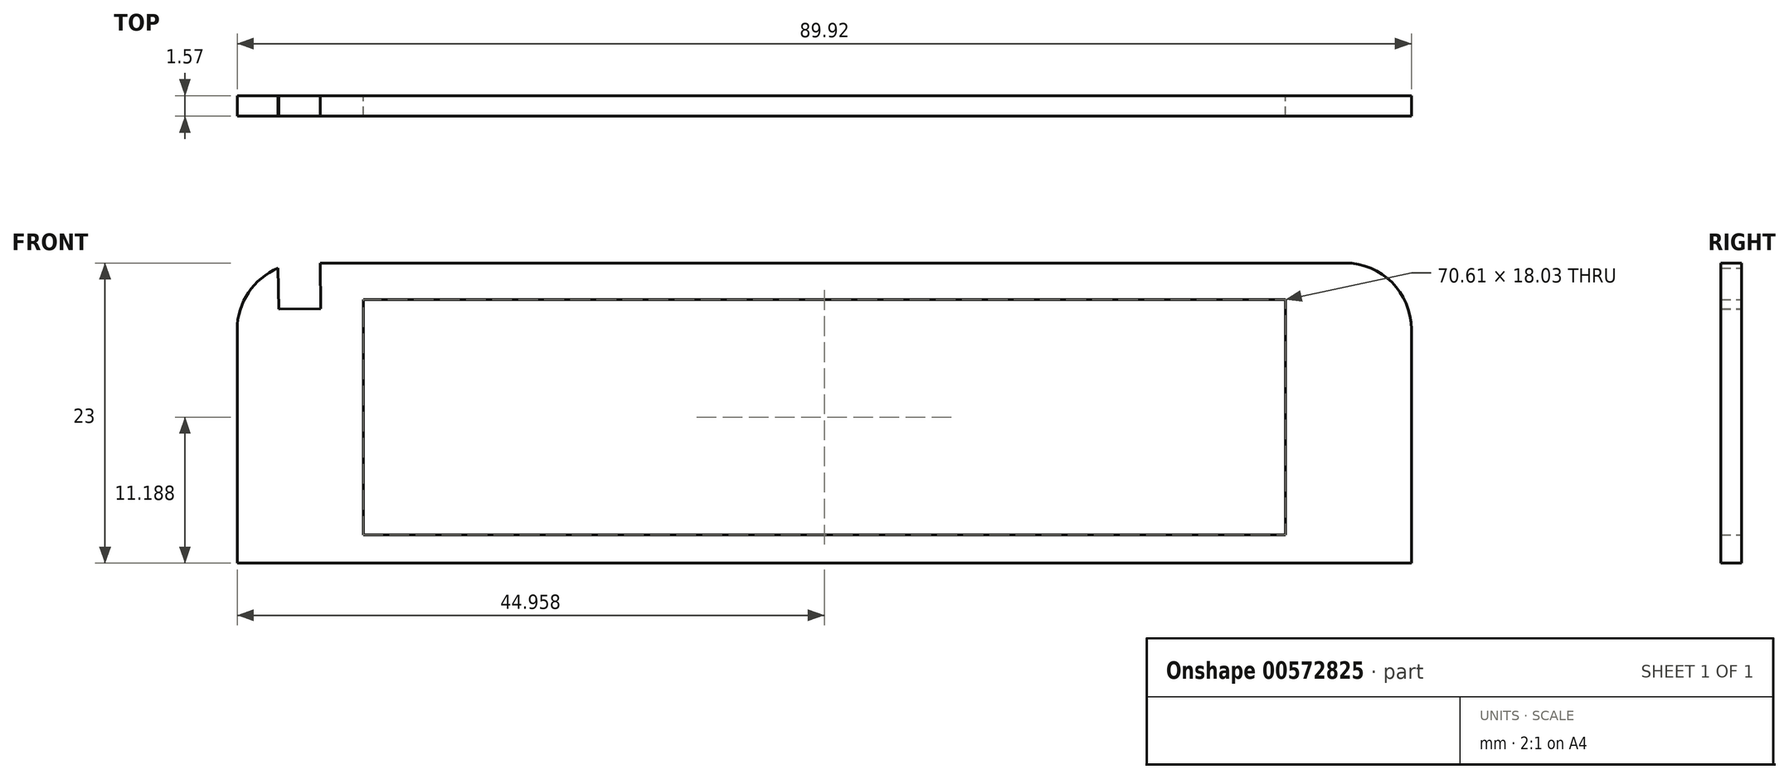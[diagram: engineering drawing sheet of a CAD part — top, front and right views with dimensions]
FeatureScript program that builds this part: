
annotation { "Feature Type Name" : "Feature", "Feature Type Description" : "" }
export const myFeature = defineFeature(function(context is Context, id is Id, definition is map)
    precondition{}
    {
        {
            var Q0;
            Q0=qCreatedBy(makeId("Front.planeOp"),FACE);
            var sketch = newSketch(context, id + "F0", { "sketchPlane" : qUnion([Q0])});
            skLineSegment(sketch, "E0.bottom", {"start": v(-35.48, 12.6) * mm, "end": v(43, 12.6) * mm});
            skPoint(sketch, "E0.middle", {"position": v(0, 0) * mm});
            skLineSegment(sketch, "E1.bottom", {"start": v(-32.18, 9.8) * mm, "end": v(38.43, 9.8) * mm});
            skLineSegment(sketch, "E1.top", {"start": v(-32.18, -8.23) * mm, "end": v(38.43, -8.23) * mm});
            skLineSegment(sketch, "E1.left", {"start": v(-32.18, 9.8) * mm, "end": v(-32.18, -8.23) * mm});
            skLineSegment(sketch, "E1.right", {"start": v(38.43, 9.8) * mm, "end": v(38.43, -8.23) * mm});
            skLineSegment(sketch, "E2", {"start": v(-41.83, -10.4) * mm, "end": v(-41.83, 7.52) * mm});
            skLineSegment(sketch, "E3", {"start": v(-41.83, -10.4) * mm, "end": v(48.09, -10.4) * mm});
            skLineSegment(sketch, "E4", {"start": v(48.09, -10.4) * mm, "end": v(48.09, 7.52) * mm});
            skPoint(sketch, "E5.visualSharp", {"position": v(48.09, 12.6) * mm});
            skArc(sketch, "E5.filletArc", {"start": v(48.09, 7.52) * mm, "mid": v(46.6, 11.11) * mm, "end": v(43, 12.6) * mm});
            skArc(sketch, "E6", {"start": v(-41.83, 7.52) * mm, "mid": v(-40.97, 10.33) * mm, "end": v(-38.7, 12.2) * mm});
            skLineSegment(sketch, "E7", {"start": v(-38.65, 9.06) * mm, "end": v(-38.7, 12.2) * mm});
            skLineSegment(sketch, "E8", {"start": v(-38.65, 9.06) * mm, "end": v(-35.42, 9.1) * mm});
            skLineSegment(sketch, "E9", {"start": v(-35.42, 9.1) * mm, "end": v(-35.48, 12.6) * mm});
            skSolve(sketch);
        }
        {
            var Q0;
            Q0=makeQuery(id+"F0.imprint","IMPRINT",FACE,{"disambiguationData":[TD([[makeQuery(id+"F0.imprint","IMPRINT",EDGE,{"derivedFrom":sQuery(id+"F0.wireOp",EDGE,"E0.bottom")}),-1.0]])]});
            extrude(context, id + "F1", {"entities" : qUnion([Q0]), "depth" : 1.57 * mm, "offsetDistance" : 25.4 * mm});
        }
    });
